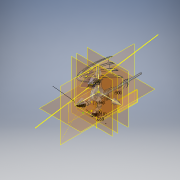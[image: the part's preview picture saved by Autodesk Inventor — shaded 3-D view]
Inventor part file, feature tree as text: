
AUTODESK INVENTOR PART (.ipt)
format: ipt  version: 2018 (Build 220112000, 112)  size: 6,354,432 bytes
history: native  units: in
note: dims shown in document units (in); Inventor stores cm internally (conversion verified against a paired STEP export)
features: sketch x129, plane x69, loft x37, fillet x16, other x16, mirror x13, projected_geometry x11, extrude x10, revolve x3, chamfer x2
ambient origin geometry x8: Origin, YZ Plane, XZ Plane, XY Plane, X Axis, Y Axis, Z Axis, Center Point
bodies: Solid1 (feature_tree)
feature tree (306):
  sketch  "Sketch4"  dims[d4=0.4in d5=0.4in]
  sketch  "Sketch5"  dims[d6=0.0in d7=0.0in]
  plane  "Work Plane2"
  loft  "Loft1"
  plane  "Work Plane4"
  sketch  "Sketch8"  dims[d10=0.0in d11=0.0in]
  plane  "Work Plane5"
  loft  "Loft2"
  extrude  "Extrusion1"  Depth=0.55in
  plane  "Work Plane6"
  extrude  "Extrusion2"  TaperAngle=0.0deg  [1 undecoded]
  extrude  "Extrusion3"  TaperAngle=0.0deg  [1 undecoded]
  chamfer  "Chamfer1"  Angle=90.0deg  [1 undecoded]
  sketch  "Sketch22"  dims[d39=0.45in d40=0.35in]
  plane  "Work Plane13"
  sketch  "Sketch23"  dims[d41=0.35in d42=0.5in]
  plane  "Work Plane14"
  loft  "Loft4"
  sketch  "Sketch25"  dims[d46=0.55in d47=0.0in]
  sketch  "Sketch26"  dims[d48=0.0in d49=0.35in d50=0.5in d51=0.0in d52=0.0in d53=90.0deg d54=0.0in d55=90.0deg d56=0.0in d57=90.0deg d58=1.0in]
  plane  "Work Plane15"
  sketch  "Sketch27"  dims[d59=1.0in d60=0.0in d61=0.25in]
  plane  "Work Plane16"
  loft  "Loft5"
  fillet  "Fillet1"  [1 undecoded]
  plane  "Work Plane17"
  sketch  "Sketch29"  dims[d64=1.2in d65=0.125in d66=0.15in d67=1.0in d68=0.0in d69=0.125in d70=0.0in]
  plane  "Work Plane18"
  sketch  "Sketch30"  dims[d75=0.03in d76=0.125in d77=45.0deg d103=0.1in]
  loft  "Loft7"
  sketch  "Sketch32"  dims[d107=0.55in d108=-0.8in]
  plane  "Work Plane21"
  sketch  "Sketch35"  dims[d109=0.5in d110=0.5in]
  plane  "Work Plane22"
  loft  "Loft8"
  plane  "Work Plane23"
  sketch  "Sketch37"  dims[d112=0.89in d113=0.0in d114=90.0deg d115=0.0in d116=90.0deg]
  sketch  "Sketch38"  dims[d117=0.0in d118=90.0deg d119=0.65in d120=0.4in]
  sketch  "Sketch39"  dims[d121=0.5in d123=0.6in]
  plane  "Work Plane25"
  loft  "Loft9"
  sketch  "Sketch43"  dims[d132=0.15in d133=0.75in]
  sketch  "Sketch44"  dims[d134=0.3in d135=0.2in]
  sketch  "Sketch45"  dims[d136=0.5in d141=0.0in d142=90.0deg]
  plane  "Work Plane27"
  loft  "Loft11"
  fillet  "Fillet2"  [1 undecoded]
  other  "Work Point3"
  sketch  "Sketch48"  dims[d155=0.124in d156=90.0deg d157=-0.75in]
  sketch  "Sketch49"  dims[d158=1.0in d159=0.55in]
  plane  "Work Plane28"
  extrude  "Extrusion4"  TaperAngle=0.0deg  [1 undecoded]
  mirror  "Mirror3"
  extrude  "Extrusion6"  Depth=0.35in
  fillet  "Fillet3"  Radius=0.5in
  fillet  "Fillet4"  [1 undecoded]
  fillet  "Fillet12"  [1 undecoded]
  fillet  "Fillet9"  [1 undecoded]
  fillet  "Fillet10"  [1 undecoded]
  fillet  "Fillet11"  Radius=1.0in
  mirror  "Mirror4"
  mirror  "Mirror5"
  mirror  "Mirror6"
  plane  "Work Plane29"
  sketch  "Sketch52"  dims[d167=0.35in d168=0.7in]
  plane  "Work Plane30"
  sketch  "Sketch54"  dims[d169=0.65in d170=0.6in]
  sketch  "Sketch55"  dims[d171=0.2in d172=0.0in d173=90.0deg]
  plane  "Work Plane31"
  sketch  "Sketch56"  dims[d174=0.0in d175=90.0deg d176=0.0in d177=90.0deg d179=0.5in]
  sketch  "Sketch57"  dims[d180=-0.1in d181=0.2in]
  plane  "Work Plane34"
  sketch  "Sketch60"  dims[d182=0.28in d187=0.7in]
  loft  "Loft14"
  loft  "Loft15"
  sketch  "Sketch61"  dims[d188=0.7in d189=0.0in d190=90.0deg]
  sketch  "Sketch62"  dims[d191=0.0in d192=90.0deg d193=0.0in d194=90.0deg d196=0.125in]
  plane  "Work Plane35"
  loft  "Loft16"
  fillet  "Fillet14"  Radius=0.15in
  fillet  "Fillet15"  Radius=1.0in
  mirror  "Mirror7"
  fillet  "Fillet16"  Radius=0.125in
  sketch  "Sketch64"  dims[d200=1.25in d201=1.55in]
  sketch  "Sketch65"  dims[d202=0.175in d203=0.25in]
  plane  "Work Plane36"
  loft  "Loft17"
  loft  "Loft18"
  sketch  "Sketch70"  dims[d221=-0.45in d222=0.4in]
  plane  "Work Plane37"
  sketch  "Sketch71"  dims[d223=0.4in d224=0.0in]
  plane  "Work Plane38"
  revolve  "Revolution1"  [1 undecoded]
  extrude  "Extrusion7"  Depth=0.5in
  chamfer  "Chamfer2"  Angle=90.0deg  [1 undecoded]
  mirror  "Mirror8"
  fillet  "Fillet19"  [1 undecoded]
  plane  "Work Plane39"
  sketch  "Sketch74"  dims[d227=0.6in]
  sketch  "Sketch75"  dims[d228=0.0in]
  plane  "Work Plane40"
  revolve  "Revolution2"  [1 undecoded]
  fillet  "Fillet21"  Radius=0.4in
  sketch  "Sketch77"  dims[d232=-0.4in]
  sketch  "Sketch78"  dims[d233=0.0in]
  plane  "Work Plane41"
  sketch  "Sketch79"  dims[d234=0.0in]
  plane  "Work Plane42"
  loft  "Loft19"
  plane  "Work Plane43"
  extrude  "Extrusion8"  Depth=0.2in
  plane  "Work Plane44"
  sketch  "Sketch82"  dims[d237=0.35in]
  plane  "Work Plane45"
  sketch  "Sketch83"  dims[d238=0.525in]
  fillet  "Fillet22"  [1 undecoded]
  loft  "Loft21"
  sketch  "Sketch85"  dims[d240=0.45in]
  sketch  "Sketch86"  dims[d241=0.4in]
  sketch  "Sketch87"  dims[d256=0.3in]
  sketch  "Sketch88"  dims[d257=0.0in d258=90.0deg]
  plane  "Work Plane46"
  sketch  "Sketch89"  dims[d259=0.0in d260=90.0deg]
  plane  "Work Plane47"
  sketch  "Sketch90"  dims[d261=0.0in d262=90.0deg]
  plane  "Work Plane48"
  sketch  "Sketch91"  dims[d263=0.0in d264=90.0deg]
  other  "Work Point4"
  loft  "Loft22"
  plane  "Work Plane49"
  sketch  "Sketch92"  dims[d265=0.0in d266=90.0deg]
  other  "Work Point5"
  loft  "Loft23"
  plane  "Work Plane50"
  sketch  "Sketch93"  dims[d267=0.0in d268=90.0deg]
  other  "Work Point6"
  loft  "Loft24"
  plane  "Work Plane51"
  sketch  "Sketch94"  dims[d270=0.45in d271=0.55in d272=0.89in]
  sketch  "Sketch95"  dims[d276=0.4in]
  other  "Work Point7"
  loft  "Loft25"
  plane  "Work Plane52"
  sketch  "Sketch96"  dims[d277=0.065in]
  sketch  "Sketch97"  dims[d278=0.5in]
  other  "Work Point8"
  loft  "Loft26"
  mirror  "Mirror9"
  sketch  "Sketch98"  dims[d279=0.55in]
  sketch  "Sketch99"  dims[d280=0.5622in]
  sketch  "Sketch100"  dims[d281=0.5544in]
  plane  "Work Plane53"
  sketch  "Sketch101"  dims[d284=0.52in]
  sketch  "Sketch102"  dims[d285=0.0in d286=90.0deg]
  other  "Work Point9"
  loft  "Loft27"
  plane  "Work Plane54"
  loft  "Loft28"
  sketch  "Sketch105"  dims[d291=0.05in]
  plane  "Work Plane55"
  loft  "Loft29"
  sketch  "Sketch107"  dims[d293=0.1388in]
  plane  "Work Plane56"
  loft  "Loft30"
  sketch  "Sketch109"  dims[d295=0.4in]
  plane  "Work Plane57"
  loft  "Loft31"
  sketch  "Sketch111"  dims[d297=0.6in]
  plane  "Work Plane58"
  loft  "Loft32"
  sketch  "Sketch113"  dims[d299=0.0in d300=90.0deg]
  sketch  "Sketch114"  dims[d301=0.0in d302=90.0deg]
  plane  "Work Plane59"
  revolve  "Revolution3"  Angle=90.0deg
  extrude  "Extrusion9"  TaperAngle=0.0deg  [1 undecoded]
  mirror  "Mirror10"
  fillet  "Fillet23"  Radius=0.5in
  plane  "Work Plane60"
  sketch  "Sketch119"  dims[d306=0.8176in]
  plane  "Work Plane61"
  sketch  "Sketch120"  dims[d307=0.75in]
  plane  "Work Plane62"
  loft  "Loft33"
  loft  "Loft34"
  plane  "Work Plane65"
  sketch  "Sketch122"  dims[d309=0.3in]
  plane  "Work Plane66"
  sketch  "Sketch123"  dims[d310=0.0in d311=90.0deg]
  plane  "Work Plane68"
  sketch  "Sketch124"  dims[d312=0.0in d313=90.0deg]
  other  "Work Point10"
  loft  "Loft35"
  sketch  "Sketch126"  dims[d315=0.4in]
  sketch  "Sketch127"  dims[d316=0.75in]
  other  "Work Point11"
  loft  "Loft36"
  fillet  "Fillet24"  Radius=0.125in
  sketch  "Sketch128"  dims[d317=90.0deg]
  sketch  "Sketch129"  dims[d318=0.75in]
  other  "Work Point12"
  loft  "Loft37"
  extrude  "Extrusion10"  Depth=1.55in
  plane  "Work Plane69"
  loft  "Loft38"
  sketch  "Sketch132"  dims[d321=0.6in]
  plane  "Work Plane71"
  sketch  "Sketch133"  dims[d322=0.2in d323=0.0in]
  sketch  "Sketch134"  dims[d324=0.1in d325=0.125in d326=45.0deg]
  loft  "Loft39"
  loft  "Loft40"
  loft  "Loft41"
  loft  "Loft42"
  other  "Work Point13"
  other  "Work Point14"
  plane  "Work Plane73"
  plane  "Work Plane74"
  plane  "Work Plane75"
  mirror  "Mirror11"
  plane  "Work Plane77"
  plane  "Work Plane78"
  plane  "Work Plane79"
  mirror  "Mirror13"
  mirror  "Mirror14"
  mirror  "Mirror15"
  mirror  "Mirror16"
  extrude  "Extrusion11"  Depth=0.4in
  sketch  "Sketch146"  dims[d339=0.6in]
  plane  "Work Plane80"
  plane  "Work Plane81"
  sketch  "Sketch147"  dims[d340=1.25in]
  plane  "Work Plane82"
  plane  "Work Plane83"
  sketch  "Sketch148"  dims[d341=1.25in]
  plane  "Work Plane84"
  sketch  "Sketch149"  dims[d344=30.0deg]
  plane  "Work Plane85"
  loft  "Loft43"
  plane  "Work Plane86"
  sketch  "Sketch151"  dims[d347=1.0in d348=0.5in d349=0.5in d350=0.5in d351=0.225in d352=0.25in d353=-0.4in d354=0.2in d355=0.06in d356=0.0in d357=90.0deg d358=0.0in d359=90.0deg d360=0.5in d361=0.5in d362=0.3125in d363=0.0in d364=0.15in d365=0.02in d366=0.175in d367=-0.6in d368=0.12in d376=0.03in d377=0.25in d378=0.0in d379=90.0deg d380=0.3937in d381=90.0deg d382=0.0in d383=90.0deg d384=0.2in d385=0.45in d388=0.2in d389=0.18in d391=0.175in d392=0.555in d393=0.27in d394=0.28in d395=0.645in d396=0.655in d397=0.678in d398=0.2in d399=0.2in d401=0.3in d402=0.35in d403=0.6in d404=0.55in d405=0.325in d406=0.6in d407=0.25in d408=0.5in d409=0.2in d410=0.45in d411=0.2in d412=0.18in d413=0.175in d414=0.555in d415=0.27in d416=0.28in d417=0.645in d418=0.655in d419=0.678in d424=-0.5in d425=0.2in d426=0.45in d427=0.2in d428=0.18in d429=0.175in d430=0.555in d431=0.27in d432=0.28in d433=0.645in d434=0.655in d435=0.678in d440=0.0in d441=90.0deg d442=0.0in d443=90.0deg d444=0.0in d445=90.0deg d446=0.15in d447=0.14in d448=0.0in d449=90.0deg d450=0.0in d451=90.0deg d452=0.0in d453=90.0deg d454=0.125in d455=0.0in d456=90.0deg d457=0.0in d458=90.0deg d459=0.0in d460=90.0deg d461=0.12in d462=0.08in d463=0.2in d464=0.45in d465=0.2in d466=0.18in d467=0.175in d468=0.555in d469=0.27in d470=0.28in d471=0.645in d472=0.655in d473=0.678in d474=0.2in d476=0.3in d477=0.12in d478=0.08in d479=0.1in d480=0.6in d481=0.135in d482=0.0in d483=90.0deg d484=0.0in d485=90.0deg d486=0.0in d487=90.0deg d488=0.45in d489=0.05in d490=0.08in d491=0.1in d492=0.5in d493=0.16in d494=0.0in d495=90.0deg d496=0.0in d497=90.0deg d498=0.0in d499=90.0deg d501=0.2in d503=0.025in d505=0.2in d506=0.325in d507=0.496in d508=0.1in d510=0.2in d511=0.2in d512=0.2in d513=0.2in d514=0.275in d515=0.105in d516=0.1752in d517=0.29in d518=0.25in d519=0.275in d520=0.08in d521=0.065in d522=0.33in d523=0.3in d524=0.07in d525=0.16in d526=0.415in d527=0.04in d529=0.16in d530=0.6in d531=0.2in d532=0.0in d533=90.0deg d534=0.0in d535=90.0deg d536=0.0in d537=90.0deg d538=0.155in d539=0.65in d540=0.31in d541=0.0in d542=90.0deg d543=0.0in d544=90.0deg d545=0.0in d546=90.0deg d547=0.7in d548=0.24in d549=0.14in d550=0.0in d551=90.0deg d552=0.0in d553=90.0deg d554=0.0in d555=90.0deg d556=0.6in d557=0.22in d558=0.13in d559=0.0in d560=90.0deg d561=0.0in d562=90.0deg d563=0.0in d564=90.0deg d565=0.6in d566=0.04in d567=0.12in d568=0.0in d569=90.0deg d570=0.0in d571=90.0deg d572=0.0in d573=90.0deg d574=0.6in d575=0.24in d576=0.11in d577=0.0in d578=90.0deg d579=0.0in d580=90.0deg d581=0.0in d582=90.0deg d583=0.01in d585=0.35in d594=60.0deg d603=0.4in d604=0.2in d605=0.085in d607=0.08in d608=0.055in d611=1.0in d612=0.0in d613=0.031in d618=0.1059in d620=0.1091in d621=0.05in d623=0.75in d625=0.07in d627=0.2in d631=1.2in d632=0.01in d633=2.75in d634=0.15in d635=0.5in d636=0.255in d637=0.4in d638=0.55in d640=0.0in d642=-0.15in d643=0.07in d644=0.7in d645=0.25in d646=0.0in d647=90.0deg d650=0.0in d651=90.0deg d652=0.0in d653=90.0deg d654=0.05in d655=1.0in d656=0.05in d662=0.05in d668=-2.0in d669=0.5in d670=0.2in d671=0.08in d672=0.0in d673=90.0deg d674=0.0in d675=90.0deg d676=0.0in d677=90.0deg d678=0.06in d679=0.055in d680=0.175in d681=0.0in d682=90.0deg d683=0.0in d684=90.0deg d685=0.0in d686=90.0deg d687=0.01in d688=0.06in d689=0.05in d690=0.08in d691=0.175in d692=0.0in d693=90.0deg d694=0.0in d695=90.0deg d696=0.0in d697=90.0deg d698=0.05in d699=1.0in d700=0.0in d701=0.3in d702=0.13in d703=0.15in d704=0.15in d705=0.16in d706=0.12in d707=0.12in d708=0.14in d709=0.1in d710=0.1in d711=0.1in d712=0.1in d713=0.0in d714=90.0deg d715=0.0in d716=90.0deg d717=0.3937in d718=90.0deg d719=0.15in d720=0.15in d721=0.125in d722=0.015in d723=0.015in d724=0.0in d725=90.0deg d726=0.0in d727=90.0deg d730=0.0in d731=90.0deg d732=0.07in d733=0.07in d734=0.07in d735=0.07in d736=0.209in d737=0.05in d738=0.0in d739=0.1in d740=0.24in d741=0.076in d742=0.0in d743=0.24in d744=0.0in d745=90.0deg d746=0.0in d747=90.0deg d748=0.0in d749=90.0deg d750=0.09in d751=0.07in d752=0.365in d753=0.355in d754=0.0in d755=90.0deg d756=0.0in d757=90.0deg d758=0.0in d759=90.0deg d760=0.085in d761=0.0in d762=90.0deg d763=0.0in d764=90.0deg d765=0.0in d766=90.0deg d767=-0.9556in d768=-2.8169in d769=0.05in d770=0.15in d771=1.0in d772=0.0in d773=0.1in d774=-0.1in d775=0.55in d777=0.05in d778=0.25in d780=0.5in d781=0.255in d782=0.0in d783=0.15in d784=0.0in d785=90.0deg d786=0.0in d787=90.0deg d788=1.1811in d789=90.0deg d790=-0.25in d791=0.13in d792=0.16in d793=0.12in d794=0.12in d795=0.14in d800=0.07in d801=0.07in d802=0.07in d803=0.07in d805=0.08in d806=0.08in d807=0.08in d808=0.08in]
  sketch  "Sketch6"  dims[d8=0.55in d9=0.55in]
  sketch  "Sketch9"  dims[d12=0.5in d13=0.0in d14=90.0deg d15=0.0in d16=90.0deg]
  other  "Edges1"
  sketch  "Sketch10"  dims[d17=0.0in d18=90.0deg d19=3.0in]
  projected_geometry  "Projected Loop2"
  projected_geometry  "Projected Loop3"
  sketch  "Sketch11"  dims[d21=0.65in d34=0.0in d35=0.0in]
  projected_geometry  "Projected Loop4"
  sketch  "Sketch12"  dims[d36=0.0in d38=0.0in]
  projected_geometry  "Projected Loop5"
  sketch  "Sketch24"  dims[d43=-0.7in d44=0.35in d45=0.0in]
  sketch  "Sketch28"  dims[d62=2.0in d63=0.6in]
  sketch  "Sketch31"  dims[d104=0.5in d106=0.45in]
  plane  "Work Plane20"
  sketch  "Sketch36"  dims[d111=0.55in]
  projected_geometry  "Projected Loop8"
  sketch  "Sketch40"  dims[d124=0.0in d125=0.2in d126=0.0in d127=90.0deg]
  sketch  "Sketch41"  dims[d128=0.0in d129=90.0deg d130=0.0in d131=90.0deg]
  plane  "Work Plane26"
  sketch  "Sketch46"  dims[d143=0.0in d144=90.0deg d146=0.5in d147=0.45in d148=0.55in d149=0.89in]
  sketch  "Sketch47"  dims[d150=45.0deg d154=0.535in]
  sketch  "Sketch50"  dims[d160=0.0in d161=90.0deg d162=0.0in d163=90.0deg]
  sketch  "Sketch51"  dims[d164=0.0in d165=90.0deg d166=-0.5in]
  projected_geometry  "Projected Loop9"
  other  "Edges4"
  other  "Edges5"
  sketch  "Sketch63"  dims[d198=0.5in d199=1.2in]
  projected_geometry  "Projected Loop10"
  sketch  "Sketch66"  dims[d204=0.25in d205=0.0in d208=0.125in d209=0.0in]
  sketch  "Sketch67"  dims[d210=0.075in d211=0.05in]
  sketch  "Sketch68"  dims[d216=0.075in d217=0.05in]
  sketch  "Sketch69"  dims[d218=0.065in d219=0.065in]
  projected_geometry  "Projected Loop11"
  sketch  "Sketch72"  dims[d225=0.0in]
  sketch  "Sketch73"  dims[d226=0.45in]
  projected_geometry  "Projected Loop12"
  sketch  "Sketch76"  dims[d229=0.0in]
  sketch  "Sketch80"  dims[d235=0.0in]
  sketch  "Sketch81"  dims[d236=0.0in]
  projected_geometry  "Projected Loop13"
  sketch  "Sketch84"  dims[d239=0.35in]
  projected_geometry  "Projected Loop14"
  sketch  "Sketch103"  dims[d287=0.0in d288=90.0deg]
  sketch  "Sketch104"  dims[d289=0.0in d290=90.0deg]
  sketch  "Sketch106"  dims[d292=0.125in]
  sketch  "Sketch108"  dims[d294=0.65in]
  sketch  "Sketch110"  dims[d296=0.5in]
  sketch  "Sketch112"  dims[d298=0.2in]
  sketch  "Sketch115"  dims[d303=0.0in d304=90.0deg]
  sketch  "Sketch116"  dims[d305=0.5in]
  sketch  "Sketch121"  dims[d308=0.2in]
  other  "Edges6"
  sketch  "Sketch125"  dims[d314=0.1in]
  sketch  "Sketch130"  dims[d319=1.3in]
  sketch  "Sketch131"  dims[d320=0.45in]
  plane  "Work Plane70"
  sketch  "Sketch136"  dims[d327=0.5944in]
  sketch  "Sketch137"  dims[d330=10.0in]
  sketch  "Sketch138"  dims[d331=10.0in]
  sketch  "Sketch139"  dims[d332=2.0in]
  sketch  "Sketch140"  dims[d333=0.6252in]
  sketch  "Sketch141"  dims[d334=0.475in]
  sketch  "Sketch142"  dims[d335=0.045in]
  sketch  "Sketch143"  dims[d336=-1.0in]
  sketch  "Sketch144"  dims[d337=2.5in]
  sketch  "Sketch145"  dims[d338=0.3in]
  sketch  "Sketch150"  dims[d346=0.125in]
note: 16 required parameter values undecoded (feature->parameter linkage not recoverable at this tier; creation-order binding heuristic only, values carry confidence <= 0.55)